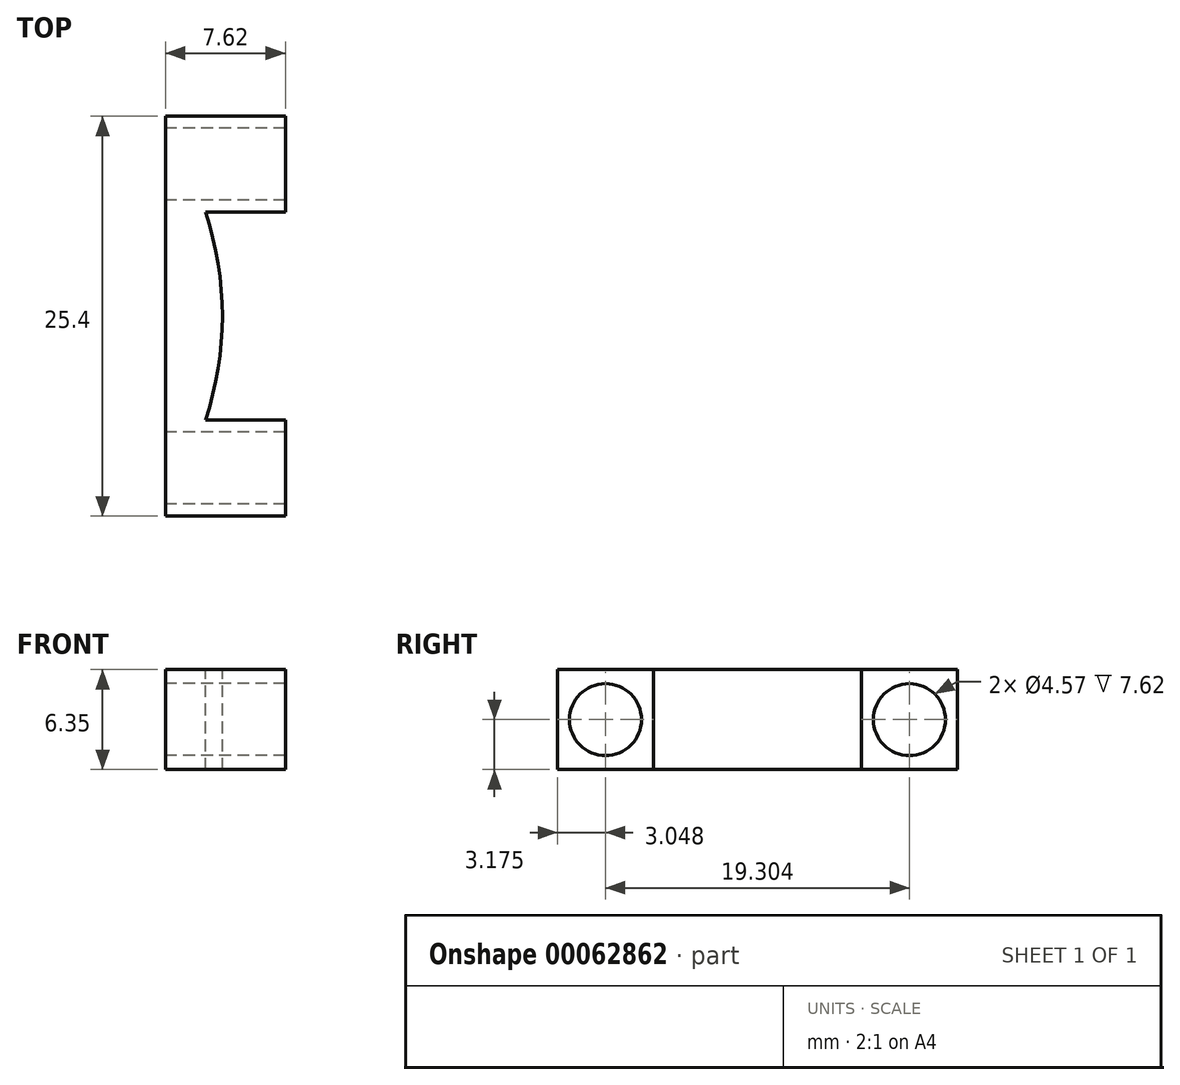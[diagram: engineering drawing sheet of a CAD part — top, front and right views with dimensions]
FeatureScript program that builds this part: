
annotation { "Feature Type Name" : "Feature", "Feature Type Description" : "" }
export const myFeature = defineFeature(function(context is Context, id is Id, definition is map)
    precondition{}
    {
        {
            var Q0;
            Q0=qCreatedBy(makeId("Top.planeOp"),FACE);
            var sketch = newSketch(context, id + "F0", { "sketchPlane" : qUnion([Q0])});
            skLineSegment(sketch, "E0.rect.bottom", {"start": v(3.8, -12.7) * mm, "end": v(-3.81, -12.7) * mm});
            skLineSegment(sketch, "E0.rect.top", {"start": v(3.81, 12.7) * mm, "end": v(-3.8, 12.7) * mm});
            skLineSegment(sketch, "E0.rect.left", {"start": v(3.8, -12.7) * mm, "end": v(3.8, 12.7) * mm});
            skPoint(sketch, "E0.rect.middle", {"position": v(0, 0) * mm});
            skLineSegment(sketch, "E1", {"start": v(-3.8, 12.7) * mm, "end": v(-3.81, -12.7) * mm});
            skSolve(sketch);
        }
        {
            var Q0;
            Q0 = qSketchRegion(id + "F0", true);
            extrude(context, id + "F1", {"entities" : qUnion([Q0]), "depth" : 6.35 * mm});
        }
        {
            var Q0;
            Q0=makeQuery(id+"F1.opExtrude","CAP_FACE",FACE,{"disambiguationData":[OSD([sQuery(id+"F0.wireOp",EDGE,"E0.rect.bottom"),sQuery(id+"F0.wireOp",EDGE,"E0.rect.top"),sQuery(id+"F0.wireOp",EDGE,"E0.rect.left"),sQuery(id+"F0.wireOp",EDGE,"E1")])],"isStart":false});
            var sketch = newSketch(context, id + "F2", { "sketchPlane" : qUnion([Q0])});
            skArc(sketch, "E2", {"start": v(-1.27, -6.6) * mm, "mid": v(-0.2, 0) * mm, "end": v(-1.27, 6.6) * mm});
            skLineSegment(sketch, "E3", {"start": v(-1.27, 6.6) * mm, "end": v(3.8, 6.6) * mm});
            skLineSegment(sketch, "E4", {"start": v(3.8, 6.6) * mm, "end": v(3.8, -6.6) * mm});
            skLineSegment(sketch, "E5", {"start": v(3.8, -6.6) * mm, "end": v(-1.27, -6.6) * mm});
            skSolve(sketch);
        }
        {
            var Q0;
            Q0=makeQuery(id+"F2.imprint","IMPRINT",FACE,{"disambiguationData":[TD([[makeQuery(id+"F2.imprint","IMPRINT",EDGE,{"derivedFrom":sQuery(id+"F2.wireOp",EDGE,"E2")}),-1.0]])]});
            extrude(context, id + "F3", {"entities" : qUnion([Q0]), "operationType" : NewBodyOperationType.REMOVE, "endBound" : BoundingType.UP_TO_NEXT, "oppositeDirection" : true, "depth" : 6.6 * mm});
        }
        {
            var Q0;
            Q0=makeQuery(id+"F1.opExtrude","SWEPT_FACE",FACE,{"disambiguationData":[OSD([sQuery(id+"F0.wireOp",EDGE,"E1")])]});
            var sketch = newSketch(context, id + "F4", { "sketchPlane" : qUnion([Q0])});
            skCircle(sketch, "E6", {"center": v(-9.65, 3.18) * mm, "radius": 2.29 * mm});
            skCircle(sketch, "E7", {"center": v(9.65, 3.18) * mm, "radius": 2.29 * mm});
            skSolve(sketch);
        }
        {
            var Q0;
            Q0 = qSketchRegion(id + "F4", true);
            extrude(context, id + "F5", {"entities" : qUnion([Q0]), "operationType" : NewBodyOperationType.REMOVE, "endBound" : BoundingType.UP_TO_NEXT, "oppositeDirection" : true, "depth" : 25.4 * mm});
        }
    });
